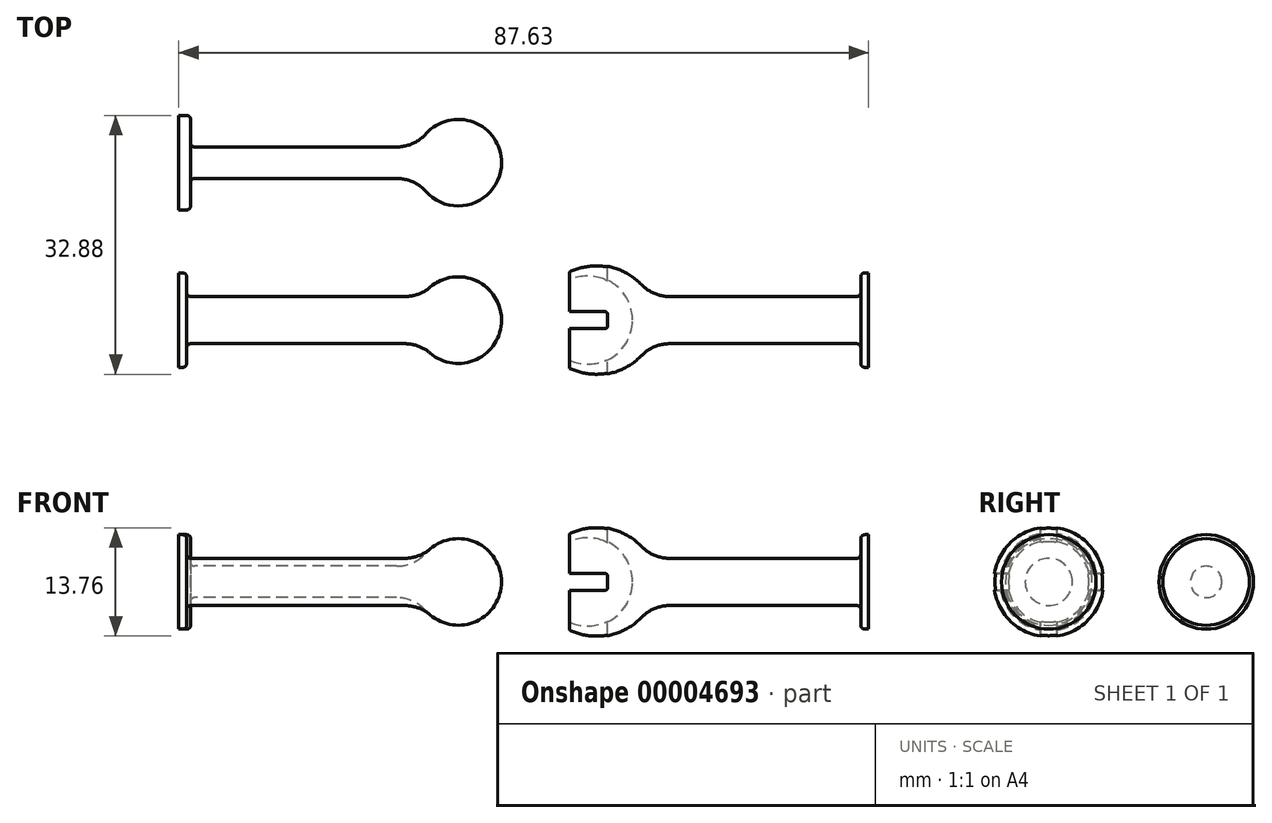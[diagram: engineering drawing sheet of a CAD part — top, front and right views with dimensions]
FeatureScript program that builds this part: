
annotation { "Feature Type Name" : "Feature", "Feature Type Description" : "" }
export const myFeature = defineFeature(function(context is Context, id is Id, definition is map)
    precondition{}
    {
        {
            var Q0;
            Q0=qCreatedBy(makeId("Top.planeOp"),FACE);
            var sketch = newSketch(context, id + "F0", { "sketchPlane" : qUnion([Q0])});
            skLineSegment(sketch, "E0", {"start": v(0, 0) * mm, "end": v(40, 0) * mm});
            skLineSegment(sketch, "E1", {"start": v(0.5, 3) * mm, "end": v(27.7, 3) * mm});
            skArc(sketch, "E2", {"start": v(40, 0) * mm, "mid": v(36.8, 5) * mm, "end": v(30.94, 4.2) * mm});
            skLineSegment(sketch, "E3", {"start": v(40, 0) * mm, "end": v(40, 5.5) * mm, "construction": true});
            skLineSegment(sketch, "E4", {"start": v(40, 5.5) * mm, "end": v(34.5, 5.5) * mm, "construction": true});
            skPoint(sketch, "E5.visualSharp", {"position": v(29.9, 3) * mm});
            skArc(sketch, "E5.filletArc", {"start": v(27.7, 3) * mm, "mid": v(29.42, 3.3) * mm, "end": v(30.94, 4.2) * mm});
            skLineSegment(sketch, "E6.bottom", {"start": v(0, 0) * mm, "end": v(-1, 0) * mm});
            skLineSegment(sketch, "E6.top", {"start": v(-0.5, 6) * mm, "end": v(-1, 6) * mm});
            skLineSegment(sketch, "E6.left", {"start": v(0, 3.5) * mm, "end": v(0, 5.5) * mm});
            skLineSegment(sketch, "E6.right", {"start": v(-1, 0) * mm, "end": v(-1, 6) * mm});
            skArc(sketch, "E7.filletArc", {"start": v(0, 3.5) * mm, "mid": v(0.15, 3.15) * mm, "end": v(0.5, 3) * mm});
            skPoint(sketch, "E8.visualSharp", {"position": v(0, 6) * mm});
            skArc(sketch, "E8.filletArc", {"start": v(0, 5.5) * mm, "mid": v(-0.15, 5.85) * mm, "end": v(-0.5, 6) * mm});
            skLineSegment(sketch, "E9", {"start": v(-1, 20) * mm, "end": v(40, 20) * mm});
            skLineSegment(sketch, "E10", {"start": v(-1, 20) * mm, "end": v(-1, 26) * mm});
            skLineSegment(sketch, "E11", {"start": v(-1, 26) * mm, "end": v(0, 26) * mm});
            skLineSegment(sketch, "E12", {"start": v(0.5, 25.5) * mm, "end": v(0.5, 22.5) * mm});
            skLineSegment(sketch, "E13", {"start": v(1, 22) * mm, "end": v(26.67, 22) * mm});
            skPoint(sketch, "E14.visualSharp", {"position": v(0.5, 26) * mm});
            skArc(sketch, "E14.filletArc", {"start": v(0.5, 25.5) * mm, "mid": v(0.36, 25.85) * mm, "end": v(0, 26) * mm});
            skPoint(sketch, "E15.visualSharp", {"position": v(0.5, 22) * mm});
            skArc(sketch, "E15.filletArc", {"start": v(0.5, 22.5) * mm, "mid": v(0.65, 22.15) * mm, "end": v(1, 22) * mm});
            skArc(sketch, "E16", {"start": v(40, 20) * mm, "mid": v(36.46, 25.14) * mm, "end": v(30.4, 23.67) * mm});
            skPoint(sketch, "E17.visualSharp", {"position": v(29.38, 22) * mm});
            skArc(sketch, "E17.filletArc", {"start": v(26.67, 22) * mm, "mid": v(28.72, 22.44) * mm, "end": v(30.4, 23.67) * mm});
            skSolve(sketch);
        }
        {
            var Q0;
            Q0=makeQuery(id+"F0.imprint","IMPRINT",FACE,{"disambiguationData":[TD([[makeQuery(id+"F0.imprint","IMPRINT",EDGE,{"derivedFrom":sQuery(id+"F0.wireOp",EDGE,"E0")}),1.0]])]});
            var Q1;
            Q1=sQuery(id+"F0.wireOp",EDGE,"E0");
            revolve(context, id + "F1", {"entities" : qUnion([Q0]), "axis" : qUnion([Q1]), "revolveType" : RevolveType.FULL});
        }
        {
            var Q0;
            Q0=qCreatedBy(makeId("Top.planeOp"),FACE);
            var sketch = newSketch(context, id + "F2", { "sketchPlane" : qUnion([Q0])});
            skLineSegment(sketch, "E18", {"start": v(56.63, 0) * mm, "end": v(86.63, 0) * mm});
            skLineSegment(sketch, "E19", {"start": v(86.63, 0) * mm, "end": v(86.63, 3) * mm});
            skArc(sketch, "E20", {"start": v(56.63, 0) * mm, "mid": v(54.04, 4.77) * mm, "end": v(48.63, 5.22) * mm});
            skLineSegment(sketch, "E21", {"start": v(56.63, 0) * mm, "end": v(56.63, 5.7) * mm, "construction": true});
            skLineSegment(sketch, "E22", {"start": v(56.63, 5.7) * mm, "end": v(50.93, 5.7) * mm, "construction": true});
            skLineSegment(sketch, "E23", {"start": v(85.13, 3) * mm, "end": v(61.36, 3) * mm});
            skArc(sketch, "E24", {"start": v(57.77, 4.53) * mm, "mid": v(53.47, 6.83) * mm, "end": v(48.63, 6.22) * mm});
            skLineSegment(sketch, "E25", {"start": v(48.63, 6.22) * mm, "end": v(48.63, 5.22) * mm});
            skPoint(sketch, "E26.visualSharp", {"position": v(58.92, 3) * mm});
            skArc(sketch, "E26.filletArc", {"start": v(57.77, 4.53) * mm, "mid": v(59.4, 3.4) * mm, "end": v(61.36, 3) * mm});
            skLineSegment(sketch, "E27.bottom", {"start": v(86.63, 0) * mm, "end": v(85.63, 0) * mm});
            skLineSegment(sketch, "E27.top", {"start": v(86.63, 6) * mm, "end": v(86.13, 6) * mm});
            skLineSegment(sketch, "E27.left", {"start": v(86.63, 0) * mm, "end": v(86.63, 6) * mm});
            skLineSegment(sketch, "E27.right", {"start": v(85.63, 3.5) * mm, "end": v(85.63, 5.5) * mm});
            skPoint(sketch, "E28.visualSharp", {"position": v(85.63, 3) * mm});
            skArc(sketch, "E28.filletArc", {"start": v(85.13, 3) * mm, "mid": v(85.49, 3.15) * mm, "end": v(85.63, 3.5) * mm});
            skPoint(sketch, "E29.visualSharp", {"position": v(85.63, 6) * mm});
            skArc(sketch, "E29.filletArc", {"start": v(86.13, 6) * mm, "mid": v(85.78, 5.85) * mm, "end": v(85.63, 5.5) * mm});
            skSolve(sketch);
        }
        {
            var Q0;
            Q0=qSketchRegion(id+"F2",true);
            var Q1;
            Q1=sQuery(id+"F2.wireOp",EDGE,"E18");
            revolve(context, id + "F3", {"entities" : qUnion([Q0]), "axis" : qUnion([Q1]), "revolveType" : RevolveType.FULL});
        }
        {
            var Q0;
            Q0=qCreatedBy(makeId("Top.planeOp"),FACE);
            cPlane(context, id + "F4", {"entities" : qUnion([Q0]), "cplaneType" : CPlaneType.OFFSET, "offset" : 50 * mm, "width" : 150 * mm, "height" : 150 * mm});
        }
        {
            var Q0;
            Q0=qCreatedBy(id+"F4.planeOp",FACE);
            var sketch = newSketch(context, id + "F5", { "sketchPlane" : qUnion([Q0])});
            skLineSegment(sketch, "E30.bottom", {"start": v(48.63, 1.07) * mm, "end": v(53.13, 1.07) * mm});
            skLineSegment(sketch, "E30.top", {"start": v(48.63, -1.07) * mm, "end": v(53.13, -1.07) * mm});
            skLineSegment(sketch, "E30.left", {"start": v(48.63, 1.07) * mm, "end": v(48.63, -1.07) * mm});
            skLineSegment(sketch, "E30.right", {"start": v(53.48, 0.72) * mm, "end": v(53.48, -0.72) * mm});
            skLineSegment(sketch, "E31", {"start": v(48.63, 0) * mm, "end": v(53.48, 0) * mm, "construction": true});
            skPoint(sketch, "E32.visualSharp", {"position": v(53.48, 1.07) * mm});
            skArc(sketch, "E32.filletArc", {"start": v(53.48, 0.72) * mm, "mid": v(53.38, 0.97) * mm, "end": v(53.13, 1.07) * mm});
            skPoint(sketch, "E33.visualSharp", {"position": v(53.48, -1.07) * mm});
            skArc(sketch, "E33.filletArc", {"start": v(53.13, -1.07) * mm, "mid": v(53.38, -0.97) * mm, "end": v(53.48, -0.72) * mm});
            skSolve(sketch);
        }
        {
            var Q0;
            Q0=makeQuery(id+"F5.imprint","IMPRINT",FACE,{"disambiguationData":[TD([[makeQuery(id+"F5.imprint","IMPRINT",EDGE,{"derivedFrom":sQuery(id+"F5.wireOp",EDGE,"E30.bottom")}),-1.0]])]});
            extrude(context, id + "F6", {"entities" : qUnion([Q0]), "endBound" : BoundingType.THROUGH_ALL, "oppositeDirection" : true, "depth" : 25 * mm});
        }
        {
            var Q0;
            Q0=makeQuery(id+"F6.opExtrude","SWEPT_BODY",BODY,{"disambiguationData":[OSD([sQuery(id+"F5.wireOp",EDGE,"E30.bottom"),sQuery(id+"F5.wireOp",EDGE,"E30.top"),sQuery(id+"F5.wireOp",EDGE,"E30.left"),sQuery(id+"F5.wireOp",EDGE,"E30.right"),sQuery(id+"F5.wireOp",EDGE,"E32.filletArc"),sQuery(id+"F5.wireOp",EDGE,"E33.filletArc")])]});
            var Q1;
            Q1=makeQuery(id+"F3.opRevolve","SWEPT_EDGE",EDGE,{"disambiguationData":[OSD([sQuery(id+"F2.wireOp",EDGE,"E20"),sQuery(id+"F2.wireOp",EDGE,"E25")])]});
            circularPattern(context, id + "F7", {"entities" : qUnion([Q0]), "axis" : qUnion([Q1]), "angle" : 90 * degree, "instanceCount" : 2});
        }
        {
            var Q0;
            Q0=makeQuery(id+"F7.opPattern","COPY",BODY,{"derivedFrom":makeQuery(id+"F6.opExtrude","SWEPT_BODY",BODY,{"disambiguationData":[OSD([sQuery(id+"F5.wireOp",EDGE,"E30.bottom"),sQuery(id+"F5.wireOp",EDGE,"E30.top"),sQuery(id+"F5.wireOp",EDGE,"E30.left"),sQuery(id+"F5.wireOp",EDGE,"E30.right"),sQuery(id+"F5.wireOp",EDGE,"E32.filletArc"),sQuery(id+"F5.wireOp",EDGE,"E33.filletArc")])]}),"instanceName":"1"});
            var Q1;
            Q1=makeQuery(id+"F6.opExtrude","SWEPT_BODY",BODY,{"disambiguationData":[OSD([sQuery(id+"F5.wireOp",EDGE,"E30.bottom"),sQuery(id+"F5.wireOp",EDGE,"E30.top"),sQuery(id+"F5.wireOp",EDGE,"E30.left"),sQuery(id+"F5.wireOp",EDGE,"E30.right"),sQuery(id+"F5.wireOp",EDGE,"E32.filletArc"),sQuery(id+"F5.wireOp",EDGE,"E33.filletArc")])]});
            var Q2;
            Q2=makeQuery(id+"F3.opRevolve","SWEPT_BODY",BODY,{"disambiguationData":[OSD([sQuery(id+"F2.wireOp",EDGE,"E18"),sQuery(id+"F2.wireOp",EDGE,"E19"),sQuery(id+"F2.wireOp",EDGE,"E20"),sQuery(id+"F2.wireOp",EDGE,"E23"),sQuery(id+"F2.wireOp",EDGE,"E24"),sQuery(id+"F2.wireOp",EDGE,"E25"),sQuery(id+"F2.wireOp",EDGE,"E26.filletArc")])]});
            booleanBodies(context, id + "F8", {"operationType" : BooleanOperationType.SUBTRACTION, "tools" : qUnion([Q0, Q1]), "targets" : qUnion([Q2])});
        }
        {
            var Q0;
            Q0=makeQuery(id+"F0.imprint","IMPRINT",FACE,{"disambiguationData":[TD([[makeQuery(id+"F0.imprint","IMPRINT",EDGE,{"derivedFrom":sQuery(id+"F0.wireOp",EDGE,"E9")}),1.0]])]});
            var Q1;
            Q1=sQuery(id+"F0.wireOp",EDGE,"E9");
            revolve(context, id + "F9", {"entities" : qUnion([Q0]), "axis" : qUnion([Q1]), "revolveType" : RevolveType.FULL});
        }
    });
